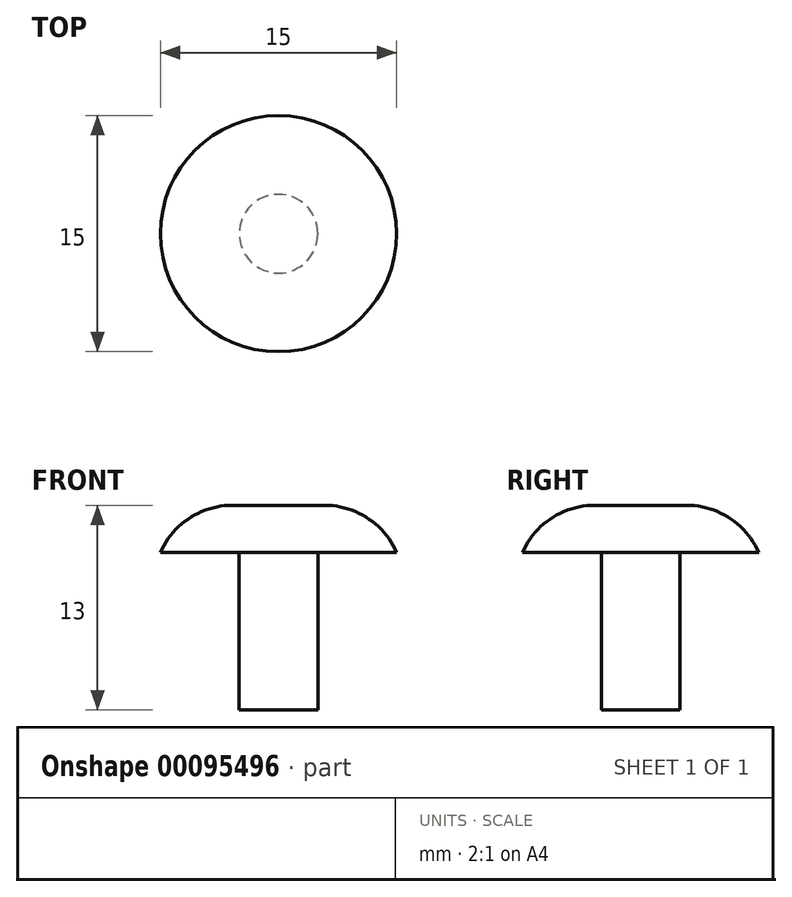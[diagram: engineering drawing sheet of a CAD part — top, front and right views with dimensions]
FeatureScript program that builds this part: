
annotation { "Feature Type Name" : "Feature", "Feature Type Description" : "" }
export const myFeature = defineFeature(function(context is Context, id is Id, definition is map)
    precondition{}
    {
        {
            var Q0;
            Q0=qCreatedBy(makeId("Top.planeOp"),FACE);
            var sketch = newSketch(context, id + "F0", { "sketchPlane" : qUnion([Q0])});
            skCircle(sketch, "E0", {"center": v(0, 0) * mm, "radius": 7.5 * mm});
            skSolve(sketch);
        }
        {
            var Q0;
            Q0=makeQuery(id+"F0.imprint","IMPRINT",FACE,{"disambiguationData":[TD([[makeQuery(id+"F0.imprint","IMPRINT",EDGE,{"derivedFrom":sQuery(id+"F0.wireOp",EDGE,"E0")}),1.0]])]});
            extrude(context, id + "F1", {"entities" : qUnion([Q0]), "depth" : 3 * mm});
        }
        {
            var Q0;
            Q0=makeQuery(id+"F1.opExtrude","CAP_FACE",FACE,{"disambiguationData":[OSD([sQuery(id+"F0.wireOp",EDGE,"E0")])],"isStart":false});
            fillet(context, id + "F2", {"entities" : qUnion([Q0]), "radius" : 5 * mm, "tangentPropagation" : true, "allowEdgeOverflow" : false});
        }
        {
            var Q0;
            Q0=qCreatedBy(makeId("Top.planeOp"),FACE);
            var sketch = newSketch(context, id + "F3", { "sketchPlane" : qUnion([Q0])});
            skCircle(sketch, "E1", {"center": v(0, 0) * mm, "radius": 2.5 * mm});
            skSolve(sketch);
        }
        {
            var Q0;
            Q0=makeQuery(id+"F3.imprint","IMPRINT",FACE,{"disambiguationData":[TD([[makeQuery(id+"F3.imprint","IMPRINT",EDGE,{"derivedFrom":sQuery(id+"F3.wireOp",EDGE,"E1")}),1.0]])]});
            extrude(context, id + "F4", {"entities" : qUnion([Q0]), "operationType" : NewBodyOperationType.ADD, "oppositeDirection" : true, "depth" : 10 * mm});
        }
    });
